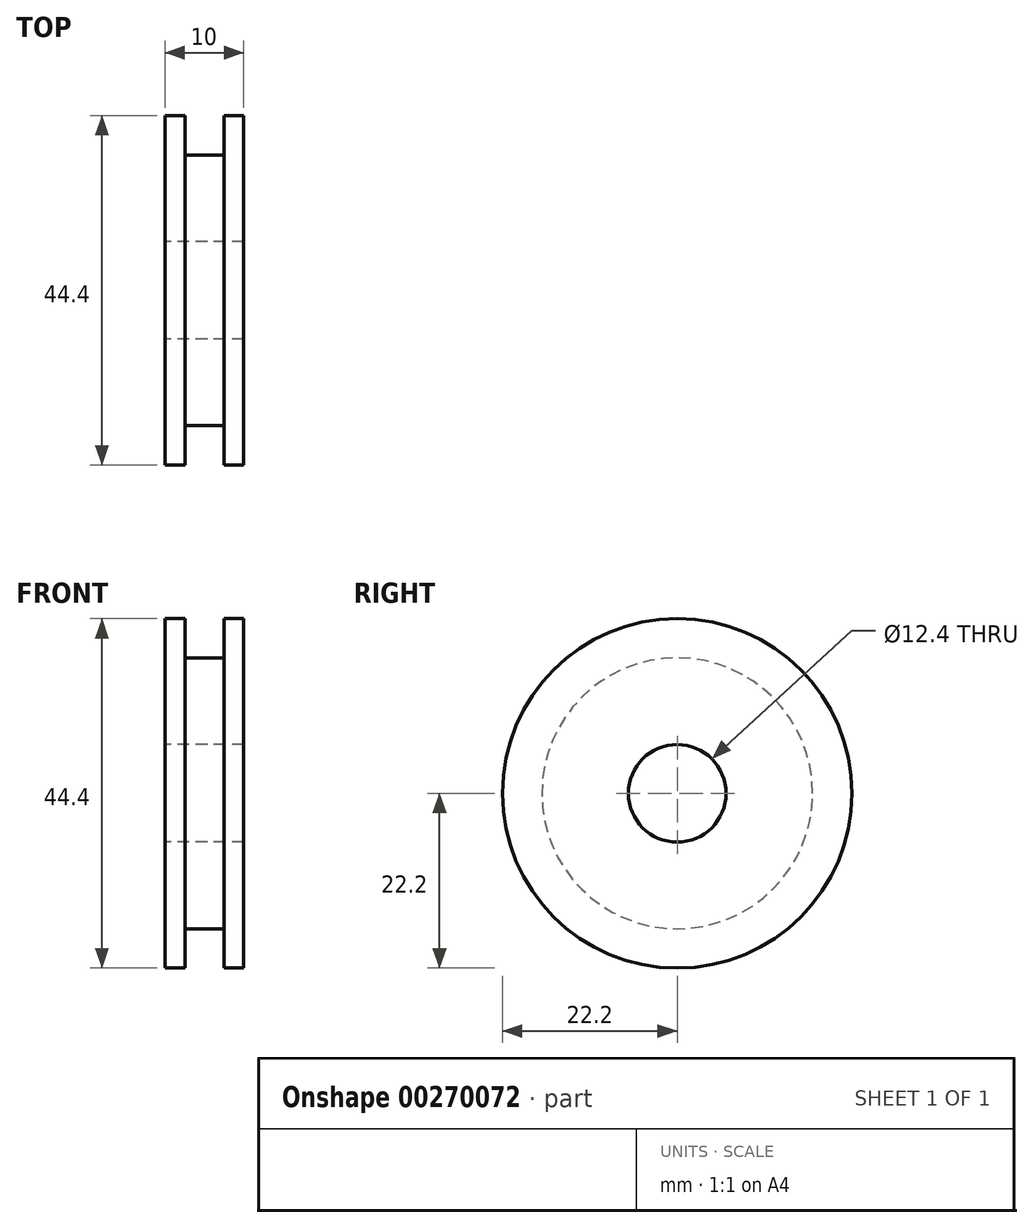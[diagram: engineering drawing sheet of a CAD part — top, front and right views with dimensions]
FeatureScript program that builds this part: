
annotation { "Feature Type Name" : "Feature", "Feature Type Description" : "" }
export const myFeature = defineFeature(function(context is Context, id is Id, definition is map)
    precondition{}
    {
        {
            var Q0;
            Q0=qCreatedBy(makeId("Top.planeOp"),FACE);
            var sketch = newSketch(context, id + "F0", { "sketchPlane" : qUnion([Q0])});
            skLineSegment(sketch, "E0.bottom", {"start": v(0, 6.2) * mm, "end": v(10, 6.2) * mm});
            skLineSegment(sketch, "E0.top", {"start": v(0, 22.2) * mm, "end": v(2.54, 22.2) * mm});
            skLineSegment(sketch, "E0.left", {"start": v(0, 6.2) * mm, "end": v(0, 22.2) * mm});
            skLineSegment(sketch, "E0.right", {"start": v(10, 6.2) * mm, "end": v(10, 22.2) * mm});
            skLineSegment(sketch, "E1.top", {"start": v(2.54, 17.2) * mm, "end": v(7.54, 17.2) * mm});
            skLineSegment(sketch, "E1.left", {"start": v(2.54, 22.2) * mm, "end": v(2.54, 17.2) * mm});
            skLineSegment(sketch, "E1.right", {"start": v(7.54, 22.2) * mm, "end": v(7.54, 17.2) * mm});
            skLineSegment(sketch, "E2.trimOffspring", {"start": v(7.54, 22.2) * mm, "end": v(10, 22.2) * mm});
            skSolve(sketch);
        }
        {
            var Q0;
            Q0=makeQuery(id+"F0.imprint","IMPRINT",FACE,{"disambiguationData":[TD([[makeQuery(id+"F0.imprint","IMPRINT",EDGE,{"derivedFrom":sQuery(id+"F0.wireOp",EDGE,"E0.bottom")}),1.0]])]});
            var sketch = newSketch(context, id + "F1", { "sketchPlane" : qUnion([Q0])});
            skLineSegment(sketch, "E3", {"start": v(-7.5, 0) * mm, "end": v(17.65, 0) * mm, "construction": true});
            skSolve(sketch);
        }
        {
            var Q0;
            Q0=makeQuery(id+"F0.imprint","IMPRINT",FACE,{"disambiguationData":[TD([[makeQuery(id+"F0.imprint","IMPRINT",EDGE,{"derivedFrom":sQuery(id+"F0.wireOp",EDGE,"E0.bottom")}),1.0]])]});
            var Q1;
            Q1=sQuery(id+"F1.wireOp",EDGE,"E3");
            revolve(context, id + "F2", {"entities" : qUnion([Q0]), "axis" : qUnion([Q1]), "revolveType" : RevolveType.FULL});
        }
    });
